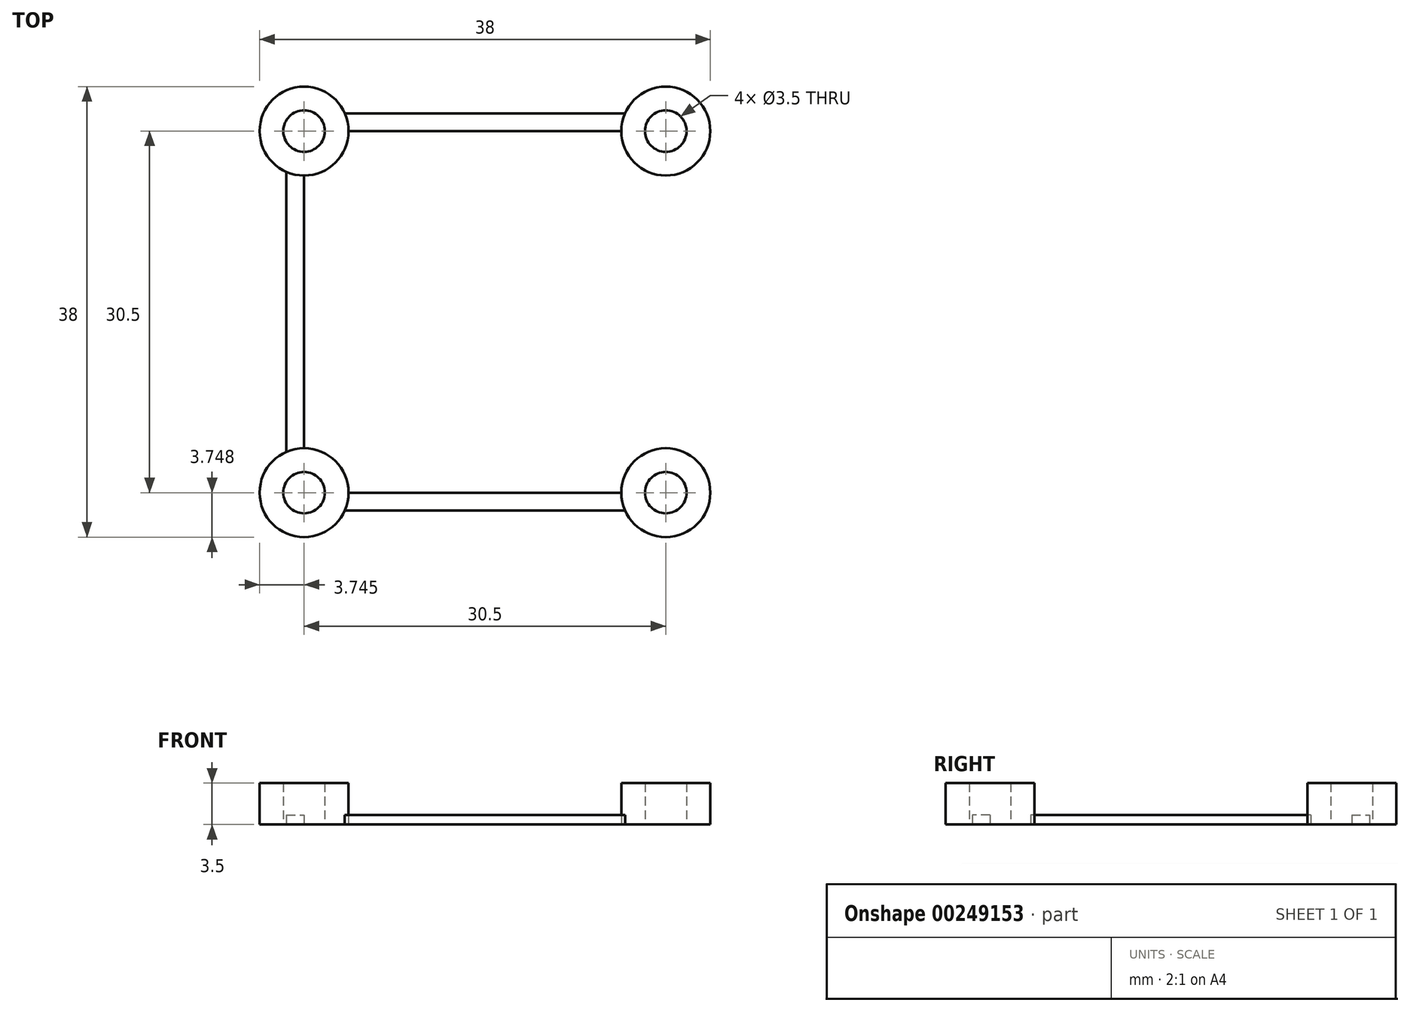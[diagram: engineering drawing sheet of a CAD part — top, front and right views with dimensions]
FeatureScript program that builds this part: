
annotation { "Feature Type Name" : "Feature", "Feature Type Description" : "" }
export const myFeature = defineFeature(function(context is Context, id is Id, definition is map)
    precondition{}
    {
        {
            var Q0;
            Q0=qCreatedBy(makeId("Top.planeOp"),FACE);
            var sketch = newSketch(context, id + "F0", { "sketchPlane" : qUnion([Q0])});
            skPoint(sketch, "E0", {"position": v(-15.68, 14.67) * mm});
            skPoint(sketch, "E1", {"position": v(14.82, 14.67) * mm});
            skPoint(sketch, "E2", {"position": v(14.82, -15.83) * mm});
            skPoint(sketch, "E3", {"position": v(-15.68, -15.83) * mm});
            skCircle(sketch, "E4", {"center": v(-15.68, 14.67) * mm, "radius": 3.75 * mm});
            skCircle(sketch, "E5", {"center": v(14.82, 14.67) * mm, "radius": 3.75 * mm});
            skCircle(sketch, "E6", {"center": v(14.82, -15.83) * mm, "radius": 3.75 * mm});
            skCircle(sketch, "E7", {"center": v(-15.68, -15.83) * mm, "radius": 3.75 * mm});
            skSolve(sketch);
        }
        {
            var Q0;
            Q0 = qSketchRegion(id + "F0", true);
            extrude(context, id + "F1", {"entities" : qUnion([Q0]), "flatOperationType" : FlatOperationType.REMOVE, "offsetDistance" : 25 * mm, "depth" : 3.5 * mm, "domain" : OperationDomain.MODEL});
        }
        {
            var Q0;
            Q0=qCreatedBy(makeId("Top.planeOp"),FACE);
            var sketch = newSketch(context, id + "F2", { "sketchPlane" : qUnion([Q0])});
            skLineSegment(sketch, "E8", {"start": v(14.82, 14.67) * mm, "end": v(-15.68, 14.67) * mm});
            skLineSegment(sketch, "E9", {"start": v(-15.68, 14.67) * mm, "end": v(-15.68, -15.83) * mm});
            skLineSegment(sketch, "E10", {"start": v(-15.68, -15.83) * mm, "end": v(14.82, -15.83) * mm});
            skLineSegment(sketch, "E11.0", {"start": v(-17.18, -17.33) * mm, "end": v(14.82, -17.33) * mm});
            skLineSegment(sketch, "E11.1", {"start": v(-17.18, 16.17) * mm, "end": v(-17.18, -17.33) * mm});
            skLineSegment(sketch, "E11.2", {"start": v(14.82, 16.17) * mm, "end": v(-17.18, 16.17) * mm});
            skLineSegment(sketch, "E12", {"start": v(14.82, 16.17) * mm, "end": v(14.82, 14.67) * mm});
            skLineSegment(sketch, "E13", {"start": v(14.82, -15.83) * mm, "end": v(14.82, -17.33) * mm});
            skSolve(sketch);
        }
        {
            var Q0;
            Q0 = qSketchRegion(id + "F2", true);
            extrude(context, id + "F3", {"entities" : qUnion([Q0]), "operationType" : NewBodyOperationType.ADD, "depth" : 0.8 * mm});
        }
        {
            var Q0;
            Q0=qCreatedBy(makeId("Top.planeOp"),FACE);
            var sketch = newSketch(context, id + "F4", { "sketchPlane" : qUnion([Q0])});
            skCircle(sketch, "E14", {"center": v(-15.68, 14.67) * mm, "radius": 1.75 * mm});
            skCircle(sketch, "E15", {"center": v(14.82, 14.67) * mm, "radius": 1.75 * mm});
            skCircle(sketch, "E16", {"center": v(14.82, -15.83) * mm, "radius": 1.75 * mm});
            skCircle(sketch, "E17", {"center": v(-15.68, -15.83) * mm, "radius": 1.75 * mm});
            skSolve(sketch);
        }
        {
            var Q0;
            Q0 = qSketchRegion(id + "F4", true);
            extrude(context, id + "F5", {"entities" : qUnion([Q0]), "operationType" : NewBodyOperationType.REMOVE, "endBound" : BoundingType.UP_TO_NEXT, "depth" : 25 * mm});
        }
    });
